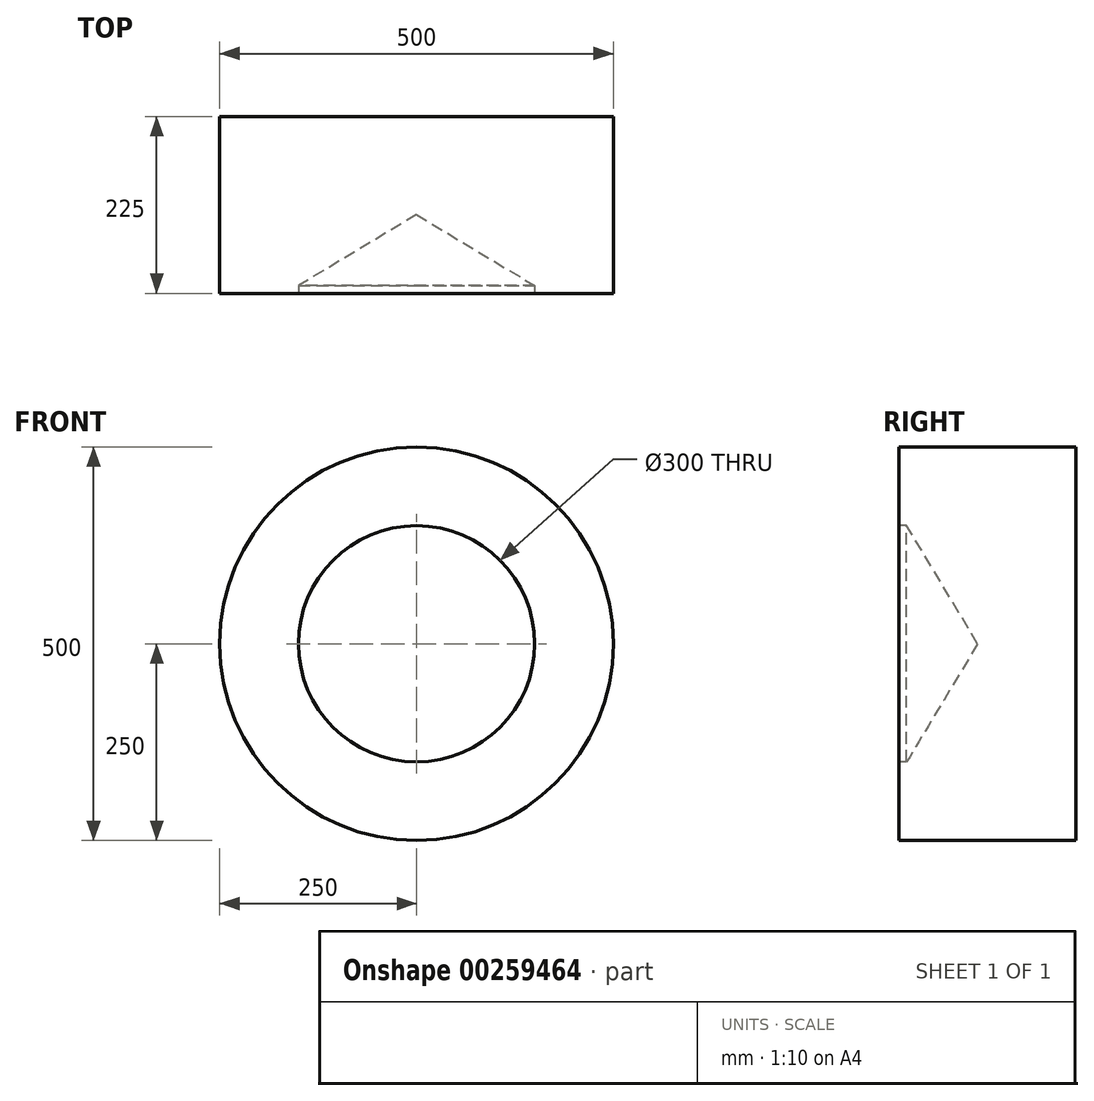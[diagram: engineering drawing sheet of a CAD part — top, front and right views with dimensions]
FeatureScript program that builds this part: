
annotation { "Feature Type Name" : "Feature", "Feature Type Description" : "" }
export const myFeature = defineFeature(function(context is Context, id is Id, definition is map)
    precondition{}
    {
        {
            var Q0;
            Q0=qCreatedBy(makeId("Front.planeOp"),FACE);
            var sketch = newSketch(context, id + "F0", { "sketchPlane" : qUnion([Q0])});
            skCircle(sketch, "E0", {"center": v(0, 0) * mm, "radius": 250 * mm});
            skSolve(sketch);
        }
        {
            var Q0;
            Q0=makeQuery(id+"F0.imprint","IMPRINT",FACE,{"disambiguationData":[TD([[makeQuery(id+"F0.imprint","IMPRINT",EDGE,{"derivedFrom":sQuery(id+"F0.wireOp",EDGE,"E0")}),1.0]])]});
            extrude(context, id + "F1", {"entities" : qUnion([Q0]), "depth" : 225 * mm});
        }
        {
            var Q0;
            Q0=makeQuery(id+"F1.opExtrude","CAP_FACE",FACE,{"disambiguationData":[OSD([sQuery(id+"F0.wireOp",EDGE,"E0")])],"isStart":false});
            var sketch = newSketch(context, id + "F2", { "sketchPlane" : qUnion([Q0])});
            skCircle(sketch, "E1", {"center": v(0, 0) * mm, "radius": 150 * mm});
            skSolve(sketch);
        }
        {
            var Q0;
            Q0=sQuery(id+"F2.wireOp",VERTEX,"E1.center");
            var Q1;
            Q1=makeQuery(id+"F1.opExtrude","SWEPT_BODY",BODY,{"disambiguationData":[OSD([sQuery(id+"F0.wireOp",EDGE,"E0")])]});
            hole(context, id + "F3", {"style" : HoleStyle.SIMPLE, "endStyle" : HoleEndStyle.BLIND, "holeDiameter" : 300 * mm, "holeDepth" : 10 * mm, "tappedDepth" : 12 * mm, "tapClearance" : 3, "startFromSketch" : true, "locations" : qUnion([Q0]), "scope" : qUnion([Q1])});
        }
    });
